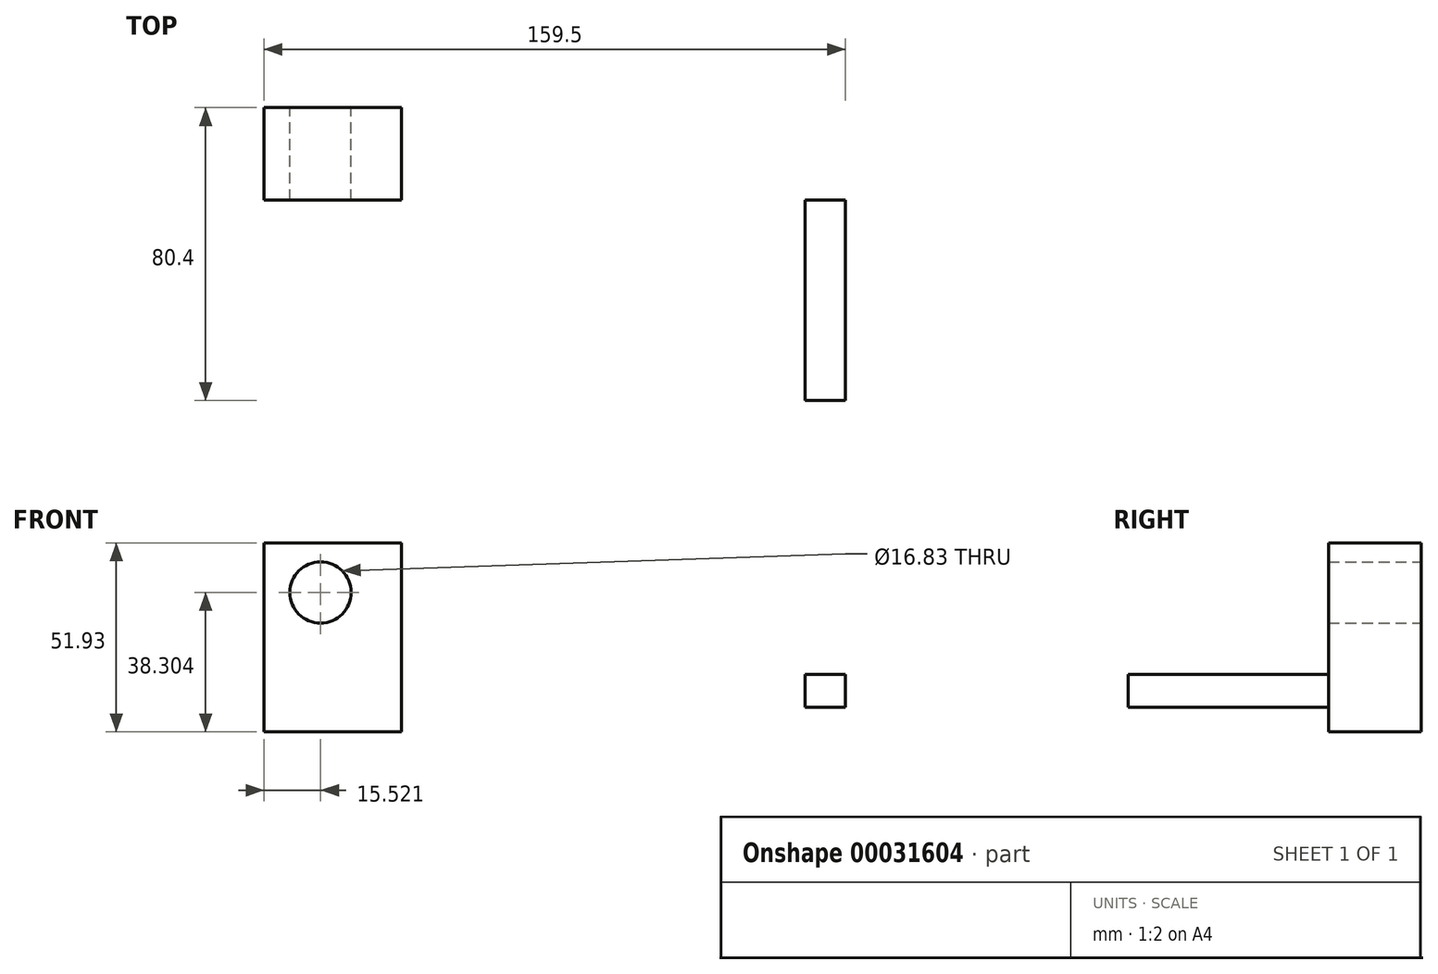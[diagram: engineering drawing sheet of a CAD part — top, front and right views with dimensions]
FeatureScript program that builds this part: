
annotation { "Feature Type Name" : "Feature", "Feature Type Description" : "" }
export const myFeature = defineFeature(function(context is Context, id is Id, definition is map)
    precondition{}
    {
        {
            var Q0;
            Q0=qCreatedBy(makeId("Front.planeOp"),FACE);
            var sketch = newSketch(context, id + "F0", { "sketchPlane" : qUnion([Q0])});
            skLineSegment(sketch, "E0.bottom", {"start": v(-107.53, 36.18) * mm, "end": v(-69.84, 36.18) * mm});
            skLineSegment(sketch, "E0.top", {"start": v(-107.53, -15.75) * mm, "end": v(-69.84, -15.75) * mm});
            skLineSegment(sketch, "E0.left", {"start": v(-107.53, 36.18) * mm, "end": v(-107.53, -15.75) * mm});
            skLineSegment(sketch, "E0.right", {"start": v(-69.84, 36.18) * mm, "end": v(-69.84, -15.75) * mm});
            skCircle(sketch, "E1", {"center": v(-92, 22.55) * mm, "radius": 8.41 * mm});
            skSolve(sketch);
        }
        {
            var Q0;
            Q0=makeQuery(id+"F0.imprint","IMPRINT",FACE,{"disambiguationData":[TD([[makeQuery(id+"F0.imprint","IMPRINT",EDGE,{"derivedFrom":sQuery(id+"F0.wireOp",EDGE,"E0.bottom")}),-1.0]])]});
            extrude(context, id + "F1", {"entities" : qUnion([Q0]), "depth" : 25.4 * mm});
        }
        {
            var Q0;
            Q0=makeQuery(id+"F1.opExtrude","CAP_FACE",FACE,{"disambiguationData":[OSD([sQuery(id+"F0.wireOp",EDGE,"E0.bottom"),sQuery(id+"F0.wireOp",EDGE,"E0.top"),sQuery(id+"F0.wireOp",EDGE,"E0.left"),sQuery(id+"F0.wireOp",EDGE,"E0.right"),sQuery(id+"F0.wireOp",EDGE,"E1")])],"isStart":false});
            var sketch = newSketch(context, id + "F3", { "sketchPlane" : qUnion([Q0])});
            skSolve(sketch);
        }
        {
            var Q0;
            Q0=makeQuery(id+"F3.imprint","IMPRINT",FACE,{"disambiguationData":[TD([[makeQuery(id+"F3.imprint","IMPRINT",EDGE,{"derivedFrom":makeQuery(id+"F1.opExtrude","CAP_EDGE",EDGE,{"disambiguationData":[OSD([sQuery(id+"F0.wireOp",EDGE,"E1")])],"isStart":false})}),1.0]])]});
            var sketch = newSketch(context, id + "F4", { "sketchPlane" : qUnion([Q0])});
            skLineSegment(sketch, "E2.bottom", {"start": v(51.97, 0) * mm, "end": v(40.93, 0) * mm});
            skLineSegment(sketch, "E2.top", {"start": v(51.97, -9) * mm, "end": v(40.93, -9) * mm});
            skLineSegment(sketch, "E2.left", {"start": v(51.97, 0) * mm, "end": v(51.97, -9) * mm});
            skLineSegment(sketch, "E2.right", {"start": v(40.93, 0) * mm, "end": v(40.93, -9) * mm});
            skLineSegment(sketch, "E3.bottom", {"start": v(5.88, 34.67) * mm, "end": v(16.23, 34.67) * mm});
            skLineSegment(sketch, "E3.top", {"start": v(5.88, 31.3) * mm, "end": v(16.23, 31.3) * mm});
            skLineSegment(sketch, "E3.left", {"start": v(5.88, 34.67) * mm, "end": v(5.88, 31.3) * mm});
            skLineSegment(sketch, "E3.right", {"start": v(16.23, 34.67) * mm, "end": v(16.23, 31.3) * mm});
            skSolve(sketch);
        }
        {
            var Q0;
            Q0=makeQuery(id+"F4.imprint","IMPRINT",FACE,{"disambiguationData":[TD([[makeQuery(id+"F4.imprint","IMPRINT",EDGE,{"derivedFrom":sQuery(id+"F4.wireOp",EDGE,"E2.bottom")}),1.0]])]});
            extrude(context, id + "F2", {"entities" : qUnion([Q0]), "depth" : 55 * mm});
        }
    });
